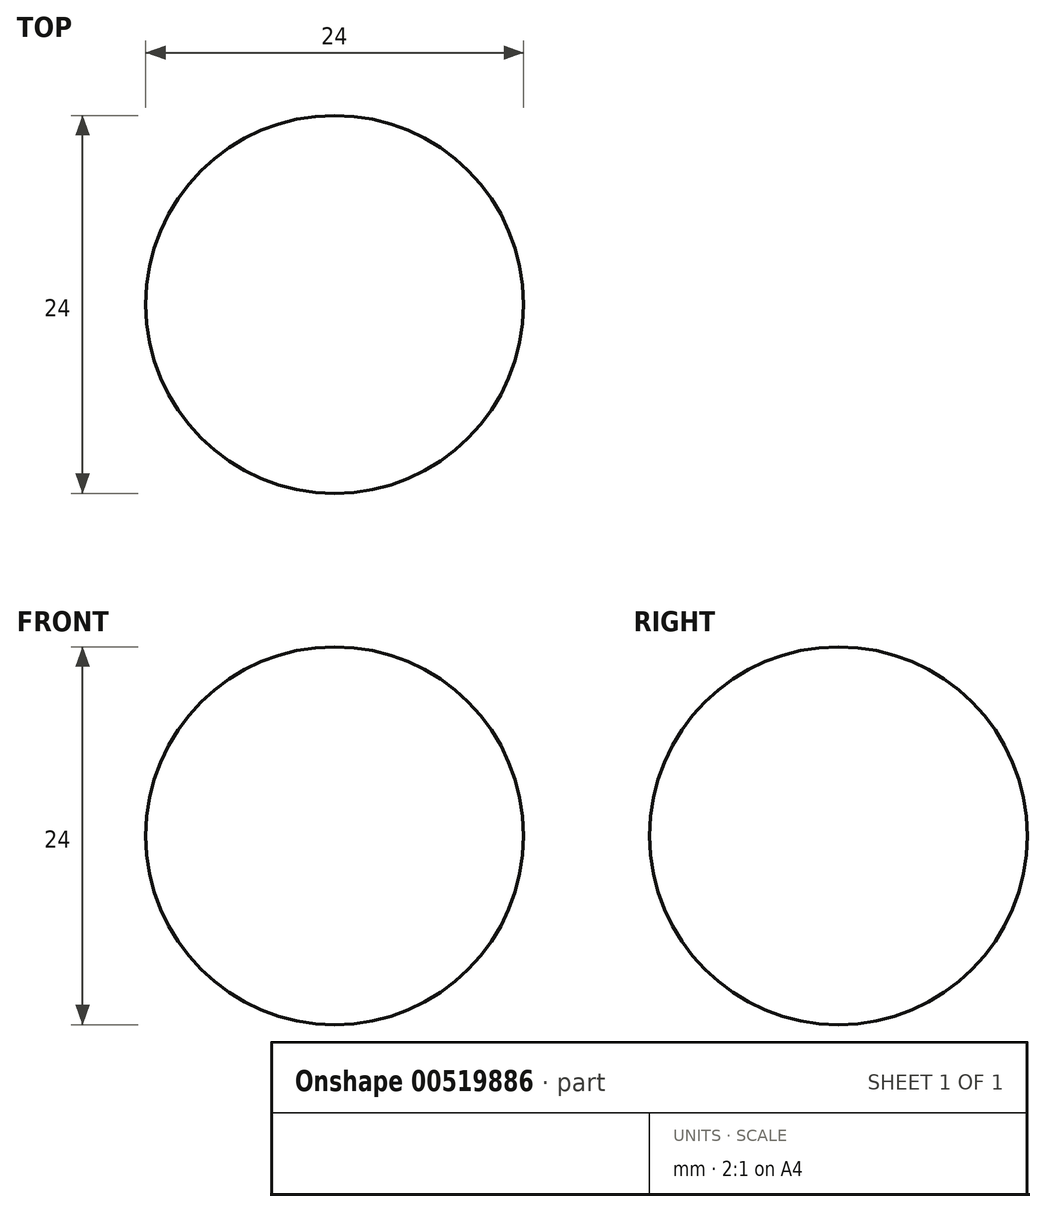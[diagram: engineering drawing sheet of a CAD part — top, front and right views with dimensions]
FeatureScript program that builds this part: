
annotation { "Feature Type Name" : "Feature", "Feature Type Description" : "" }
export const myFeature = defineFeature(function(context is Context, id is Id, definition is map)
    precondition{}
    {
        {
            var Q0;
            Q0=qCreatedBy(makeId("Top.planeOp"),FACE);
            var sketch = newSketch(context, id + "F0", { "sketchPlane" : qUnion([Q0])});
            skArc(sketch, "E0", {"start": v(0, -12) * mm, "mid": v(12, 0) * mm, "end": v(0, 12) * mm});
            skLineSegment(sketch, "E1", {"start": v(0, 16.68) * mm, "end": v(0, -26.89) * mm, "construction": true});
            skLineSegment(sketch, "E2", {"start": v(0, 12) * mm, "end": v(0, -12) * mm});
            skSolve(sketch);
        }
        {
            var Q0;
            Q0 = qSketchRegion(id + "F0", true);
            var Q1;
            Q1=sQuery(id+"F0.wireOp",EDGE,"E1");
            revolve(context, id + "F1", {"entities" : qUnion([Q0]), "axis" : qUnion([Q1]), "revolveType" : RevolveType.FULL});
        }
    });
